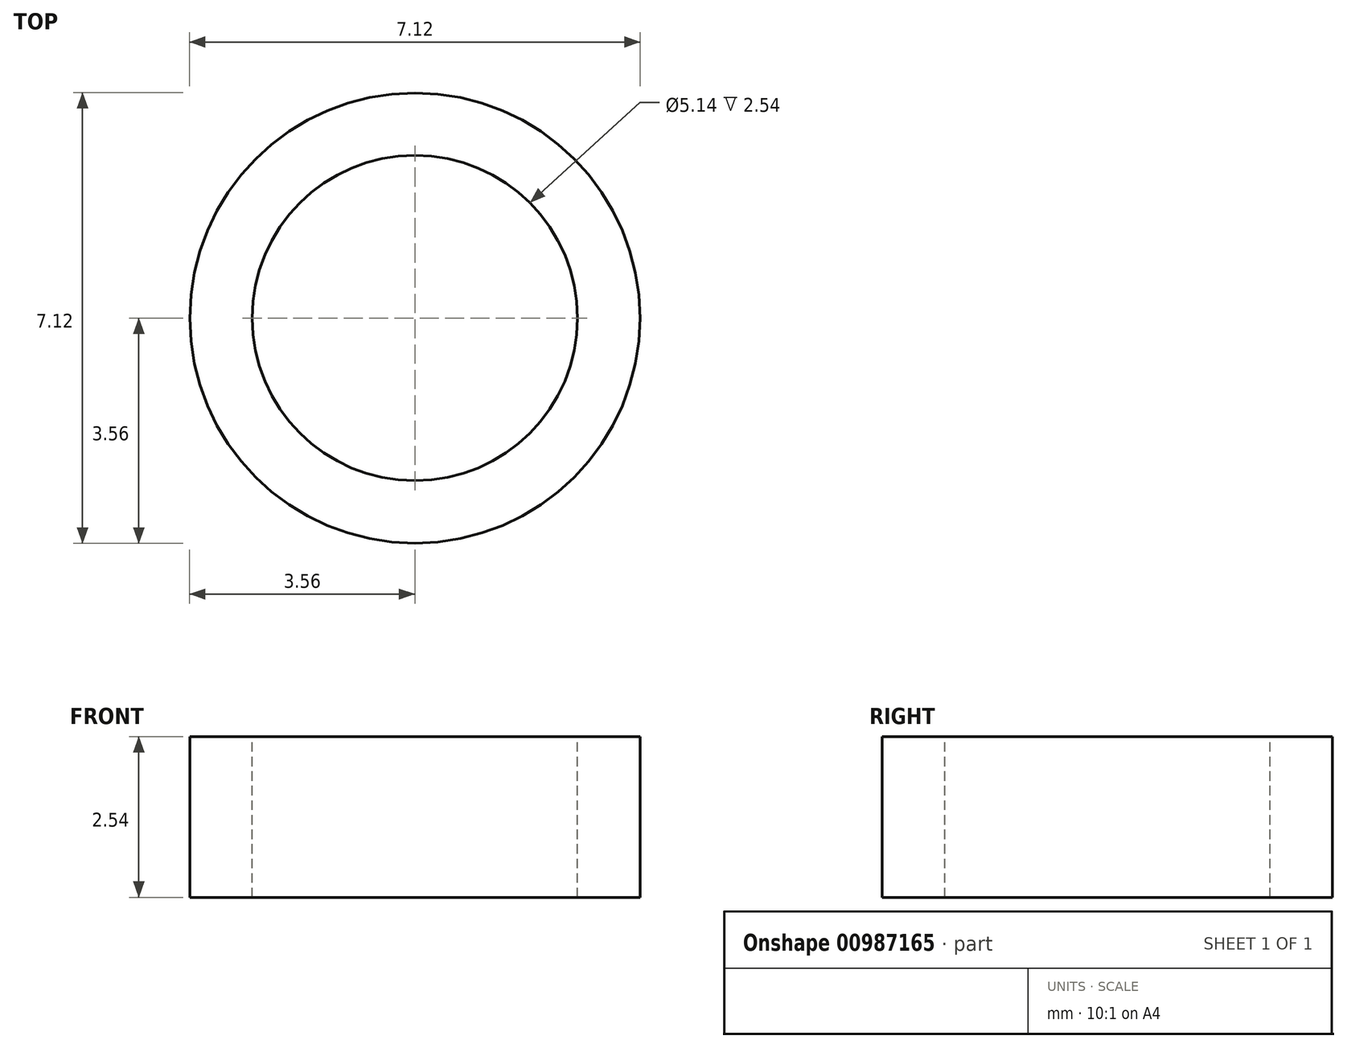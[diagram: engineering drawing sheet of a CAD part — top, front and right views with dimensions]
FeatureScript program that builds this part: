
annotation { "Feature Type Name" : "Feature", "Feature Type Description" : "" }
export const myFeature = defineFeature(function(context is Context, id is Id, definition is map)
    precondition{}
    {
        {
            var Q0;
            Q0=qCreatedBy(makeId("Top.planeOp"),FACE);
            var sketch = newSketch(context, id + "F0", { "sketchPlane" : qUnion([Q0])});
            skCircle(sketch, "E0", {"center": v(0, 0) * mm, "radius": 3.56 * mm});
            skCircle(sketch, "E1", {"center": v(0, 0) * mm, "radius": 4.06 * mm});
            skSolve(sketch);
        }
        {
            var Q0;
            Q0=makeQuery(id+"F0.imprint","IMPRINT",FACE,{"disambiguationData":[TD([[makeQuery(id+"F0.imprint","IMPRINT",EDGE,{"derivedFrom":sQuery(id+"F0.wireOp",EDGE,"E0")}),1.0]])]});
            extrude(context, id + "F1", {"entities" : qUnion([Q0]), "depth" : 2.54 * mm, "offsetDistance" : 25.4 * mm});
        }
        {
            var Q0;
            Q0=makeQuery(id+"F1.opExtrude","CAP_FACE",FACE,{"disambiguationData":[OSD([sQuery(id+"F0.wireOp",EDGE,"E0")])],"isStart":false});
            var sketch = newSketch(context, id + "F2", { "sketchPlane" : qUnion([Q0])});
            skCircle(sketch, "E2", {"center": v(0, 0) * mm, "radius": 2.57 * mm});
            skSolve(sketch);
        }
        {
            var Q0;
            Q0=makeQuery(id+"F2.imprint","IMPRINT",FACE,{"disambiguationData":[TD([[makeQuery(id+"F2.imprint","IMPRINT",EDGE,{"derivedFrom":sQuery(id+"F2.wireOp",EDGE,"E2")}),1.0]])]});
            extrude(context, id + "F3", {"entities" : qUnion([Q0]), "operationType" : NewBodyOperationType.REMOVE, "oppositeDirection" : true, "depth" : 25.4 * mm, "offsetDistance" : 25.4 * mm});
        }
    });
